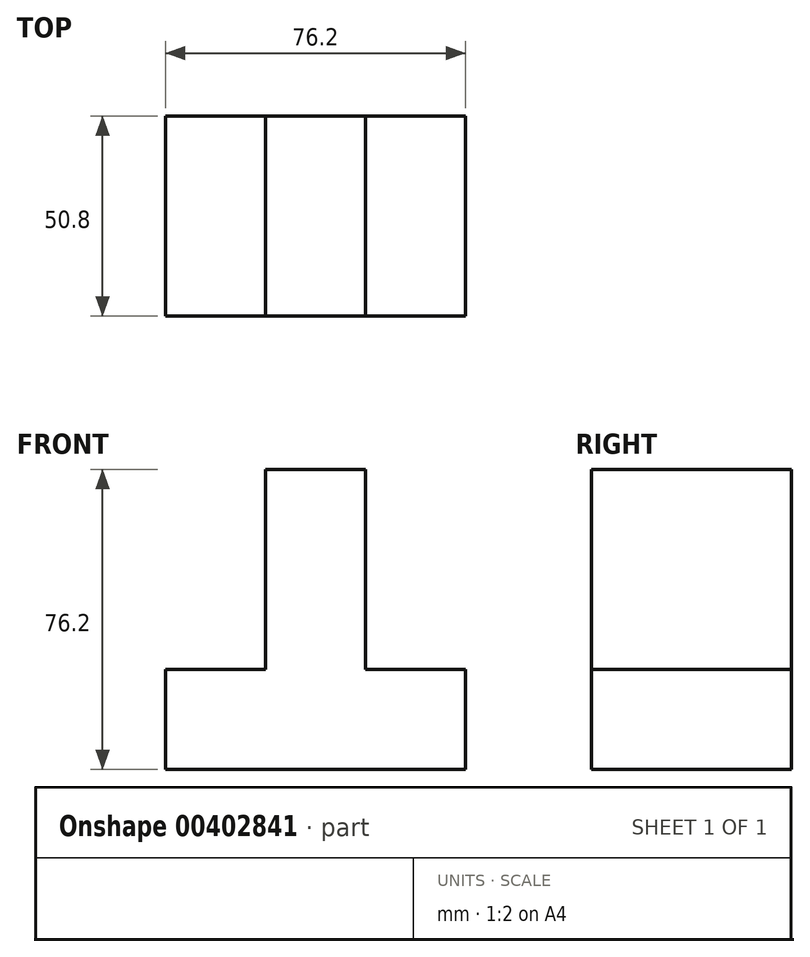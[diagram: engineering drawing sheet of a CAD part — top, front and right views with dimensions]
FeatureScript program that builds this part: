
annotation { "Feature Type Name" : "Feature", "Feature Type Description" : "" }
export const myFeature = defineFeature(function(context is Context, id is Id, definition is map)
    precondition{}
    {
        {
            var Q0;
            Q0=qCreatedBy(makeId("Front.planeOp"),FACE);
            var sketch = newSketch(context, id + "F0", { "sketchPlane" : qUnion([Q0])});
            skLineSegment(sketch, "E0", {"start": v(0, 0) * mm, "end": v(76.2, 0) * mm});
            skLineSegment(sketch, "E1", {"start": v(0, 0) * mm, "end": v(0, 25.4) * mm});
            skLineSegment(sketch, "E2", {"start": v(0, 25.4) * mm, "end": v(25.4, 25.4) * mm});
            skLineSegment(sketch, "E3", {"start": v(76.2, 0) * mm, "end": v(76.2, 25.4) * mm});
            skLineSegment(sketch, "E4", {"start": v(76.2, 25.4) * mm, "end": v(50.8, 25.4) * mm});
            skLineSegment(sketch, "E5", {"start": v(25.4, 25.4) * mm, "end": v(25.4, 76.2) * mm});
            skLineSegment(sketch, "E6", {"start": v(25.4, 76.2) * mm, "end": v(50.8, 76.2) * mm});
            skLineSegment(sketch, "E7", {"start": v(50.8, 76.2) * mm, "end": v(50.8, 25.4) * mm});
            skSolve(sketch);
        }
        {
            var Q0;
            Q0 = qSketchRegion(id + "F0", true);
            extrude(context, id + "F1", {"entities" : qUnion([Q0]), "depth" : 50.8 * mm});
        }
    });
